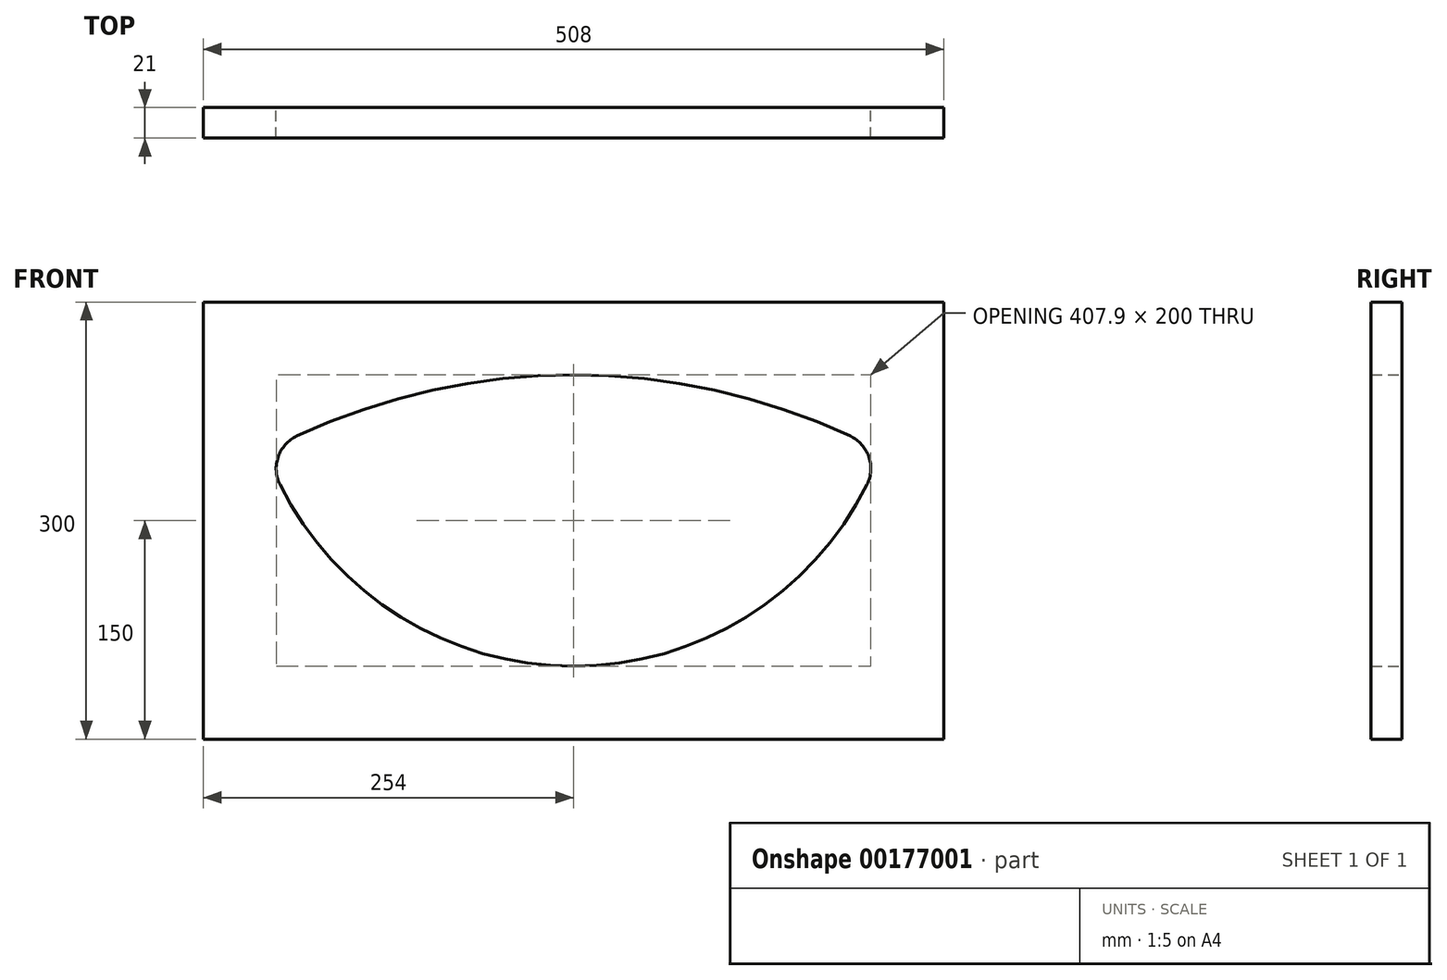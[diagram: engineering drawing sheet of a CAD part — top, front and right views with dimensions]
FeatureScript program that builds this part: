
annotation { "Feature Type Name" : "Feature", "Feature Type Description" : "" }
export const myFeature = defineFeature(function(context is Context, id is Id, definition is map)
    precondition{}
    {
        {
            var Q0;
            Q0=qCreatedBy(makeId("Front.planeOp"),FACE);
            var sketch = newSketch(context, id + "F0", { "sketchPlane" : qUnion([Q0])});
            skLineSegment(sketch, "E0.bottom", {"start": v(0, 0) * mm, "end": v(508, 0) * mm});
            skLineSegment(sketch, "E0.top", {"start": v(0, 300) * mm, "end": v(508, 300) * mm});
            skLineSegment(sketch, "E0.left", {"start": v(0, 0) * mm, "end": v(0, 300) * mm});
            skLineSegment(sketch, "E0.right", {"start": v(508, 0) * mm, "end": v(508, 300) * mm});
            skLineSegment(sketch, "E1.bottom", {"start": v(50, 250) * mm, "end": v(458, 250) * mm, "construction": true});
            skLineSegment(sketch, "E1.top", {"start": v(50, 50) * mm, "end": v(458, 50) * mm, "construction": true});
            skLineSegment(sketch, "E1.left", {"start": v(50, 250) * mm, "end": v(50, 50) * mm, "construction": true});
            skLineSegment(sketch, "E1.right", {"start": v(458, 250) * mm, "end": v(458, 50) * mm, "construction": true});
            skLineSegment(sketch, "E2", {"start": v(254, 581.91) * mm, "end": v(254, -377.3) * mm, "construction": true});
            skPoint(sketch, "E3", {"position": v(254, 300) * mm});
            skArc(sketch, "E4", {"start": v(443.75, 208.04) * mm, "mid": v(254, 250) * mm, "end": v(64.25, 208.04) * mm});
            skArc(sketch, "E5", {"start": v(52.58, 174.72) * mm, "mid": v(254, 50) * mm, "end": v(455.42, 174.72) * mm});
            skArc(sketch, "E6", {"start": v(455.42, 174.72) * mm, "mid": v(456.62, 193.84) * mm, "end": v(443.75, 208.04) * mm});
            skArc(sketch, "E7", {"start": v(64.25, 208.04) * mm, "mid": v(51.38, 193.84) * mm, "end": v(52.58, 174.72) * mm});
            skSolve(sketch);
        }
        {
            var Q0;
            Q0=makeQuery(id+"F0.imprint","IMPRINT",FACE,{"disambiguationData":[TD([[makeQuery(id+"F0.imprint","IMPRINT",EDGE,{"derivedFrom":sQuery(id+"F0.wireOp",EDGE,"E0.bottom")}),1.0]])]});
            extrude(context, id + "F1", {"entities" : qUnion([Q0]), "depth" : 21 * mm});
        }
    });
